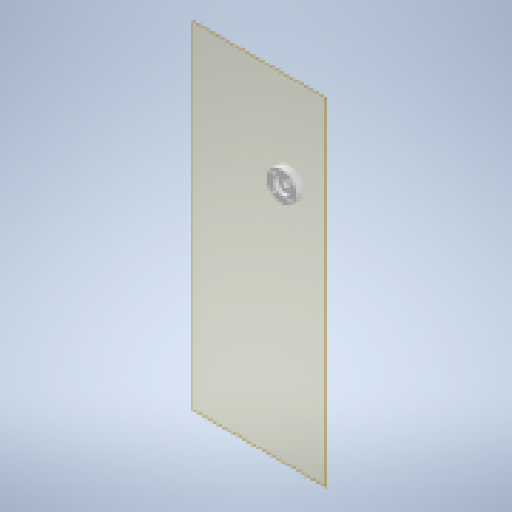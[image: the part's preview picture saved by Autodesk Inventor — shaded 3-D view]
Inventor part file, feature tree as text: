
AUTODESK INVENTOR PART (.ipt)
format: ipt  version: 2024.2 (Build 282272000, 272)  size: 143,872 bytes
history: native  units: mm
features: other x6, reference x5, extrude x2, sketch x1
ambient origin geometry x8: Origin, YZ Plane, XZ Plane, XY Plane, X Axis, Y Axis, Z Axis, Center Point
bodies: Body1 (feature_tree)
feature tree (14):
  other  "Твердое тело1"
  other  "РабПлоскость1"
  sketch  "Эскиз1"
  extrude  "Выдавливание1"  Depth=25.0mm
  extrude  "Выдавливание2"  Depth=6.0mm TaperAngle=0.0deg
  reference  "Ссылка1"
  reference  "Ссылка2"
  reference  "Ссылка3"
  reference  "Ссылка4"
  reference  "Ссылка5"
  other  "<userpath>\Documents\Artist-v2\3D\Робот.iam"
  other  "Робот.iam"
  other  "бок:1"
  other  "крепеж подшипника:2"
